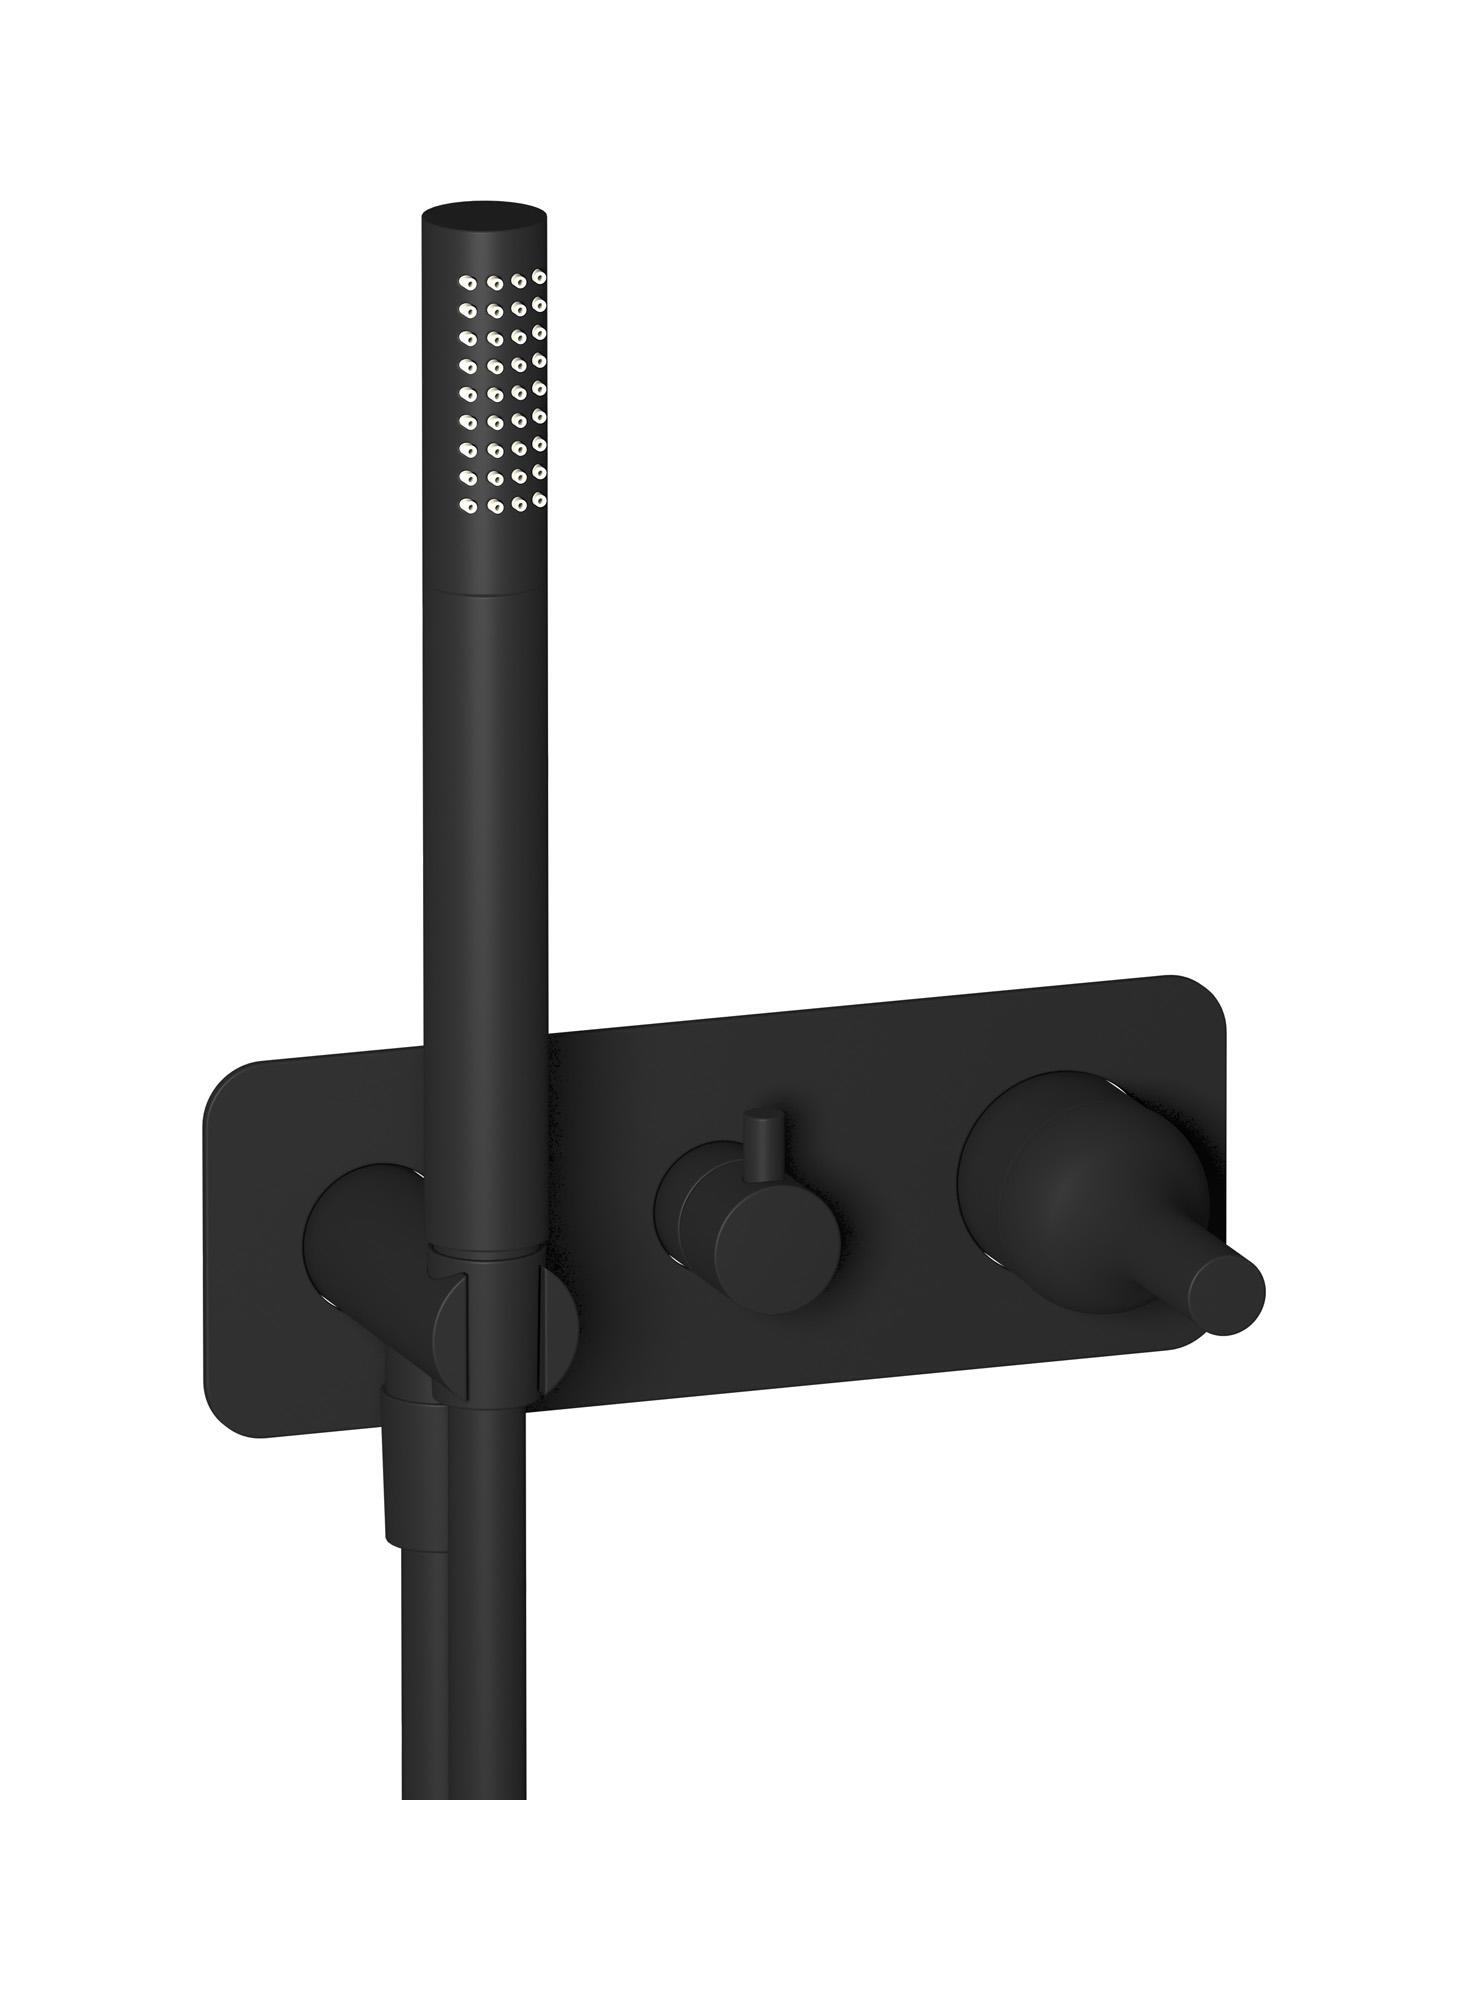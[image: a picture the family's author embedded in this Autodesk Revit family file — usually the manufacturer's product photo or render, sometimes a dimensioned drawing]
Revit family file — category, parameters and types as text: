
# Revit family: BI314
name_source: partatom
category: Apparecchi idraulici
units: mm (PartAtom-declared; Revit-internal decimal feet)

## family parameters
Basato su piano di lavoro = No
Condiviso = No
Mantieni orientamento annotazione = No
Numero OmniClass = 23.45.55.17
Punto di calcolo locali = No
Quota connettore circolare = Usa diametro
Sempre verticale = Sì
Taglio con vuoti quando caricato = No
Tipo di parte = Normale
Titolo OmniClass = Mixing Faucets

## types (4) — shared parameters
Cold water flow = 0,0 L/s
Cold water inlet = 10 mm  [stored 0.0328084 ft]
Commenti sul tipo = Wall mixer
Connessione CW = No
Connessione HW = No
Connessione di scarico = No
Connessione di ventilazione = No
Descrizione = Exposed parts for manual wall mixer with three ways diverter and shower kit
Hot water inlet = 10 mm  [stored 0.0328084 ft]
Produttore = IB Rubinetterie S.p.A.
URL = https://www.weareib.it
zero-valued in all types: Prospetto di default

## per-type parameters (varying)
| type | Finishes surface | Immagine tipo | Modello |
| Chrome | IB_Chrome | BI314CC.jpg | BI314CC |
| Brushed nickel | IB_Brushed nickel | BI314SS.jpg | BI314SS |
| Matt white | IB_matt white | BI314BO.jpg | BI314BO |
| Matt black | IB_matt black | BI314NP.jpg | BI314NP |

note: [stored X ft] marks values corroborated as IEEE doubles in the binary element streams (Revit-internal decimal feet)
